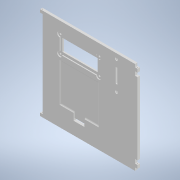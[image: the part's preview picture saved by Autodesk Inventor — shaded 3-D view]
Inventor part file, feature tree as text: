
AUTODESK INVENTOR PART (.ipt)
format: ipt  version: 2020 (Build 240168000, 168)  size: 380,928 bytes
history: native  units: in
note: dims shown in document units (in); Inventor stores cm internally (conversion verified against a paired STEP export)
features: extrude x10, sketch x8, hole x7, fillet x3, plane x2, shell x1, split x1
ambient origin geometry x8: Origin, YZ Plane, XZ Plane, XY Plane, X Axis, Y Axis, Z Axis, Center Point
bodies: Solid1 (feature_tree)
feature tree (32):
  extrude  "Extrusion1"  Depth=7.874in
  shell  "Shell1"  Thickness=7.874in
  extrude  "Extrusion2"  Depth=1.6339in
  sketch  "Sketch3"  dims[d7=6.1024in d8=1.6339in]
  extrude  "Extrusion3"  Depth=1.1811in
  hole  "Hole1"  [1 undecoded]
  fillet  "Fillet2"  Radius=0.8661in
  extrude  "Extrusion4"  Depth=1.1417in
  sketch  "Sketch4"  dims[d9=0.3937in d10=0.0in d12=1.1811in]
  extrude  "Extrusion5"  Depth=0.3937in
  extrude  "Extrusion6"  Depth=2.8346in
  extrude  "Extrusion7"  Depth=0.1575in
  extrude  "Extrusion8"  Depth=0.1575in
  fillet  "Fillet3"  Radius=0.1969in
  fillet  "Fillet4"  Radius=0.1969in
  extrude  "Extrusion9"  Depth=0.3937in
  plane  "Work Plane1"
  extrude  "Extrusion10"  Depth=0.3937in
  plane  "Work Plane2"
  split  "Split1"
  hole  "Hole3"  [1 undecoded]
  hole  "Hole4"  [1 undecoded]
  hole  "Hole5"  [1 undecoded]
  hole  "Hole6"  [1 undecoded]
  hole  "Hole7"  [1 undecoded]
  sketch  "Sketch1"  dims[d0=7.874in d1=7.874in d2=7.874in d3=0.0in]
  sketch  "Sketch5"  dims[d13=1.5748in d16=3.1496in d19=0.8661in]
  sketch  "Sketch6"  dims[d20=0.1575in d22=1.1417in]
  hole  "Hole2"  [1 undecoded]
  sketch  "Sketch7"  dims[d23=0.3937in d24=0.3937in]
  sketch  "Sketch8"  dims[d25=0.0787in d26=0.0in d27=2.8346in]
  sketch  "Sketch9"  dims[d28=0.9843in d29=0.1575in d30=0.1575in d31=0.1969in d32=0.1969in d33=0.3937in d34=0.3937in d35=0.3937in d36=0.1378in d37=0.2362in d38=0.1575in d39=0.0787in d40=90.0deg d41=0.315in d42=0.8108in d43=0.1181in d44=3.937in d45=0.1969in d46=0.0in d47=0.0787in d48=0.0591in d49=3.1496in d50=0.0in d51=2.3622in d52=0.0in d53=1.5748in d54=0.0in d55=0.7874in d56=0.0in d57=0.1181in d58=0.1575in d59=1.5748in d60=0.0in d61=-0.5906in d62=0.9843in d63=0.0in d64=0.0in d67=0.3937in d73=0.1969in d74=0.2362in d75=0.2756in d76=0.315in d77=0.2362in d78=0.2756in d79=0.315in d80=0.1969in d81=0.2362in d82=0.2362in d83=0.0787in d84=0.2362in d85=0.1575in d86=0.0787in d87=90.0deg d88=0.315in d89=0.0in d90=0.5586in d91=0.5586in d92=0.0689in d93=0.0689in d94=0.1575in d95=0.2362in d96=0.2362in d97=0.0787in d98=90.0deg d99=0.5906in d100=0.0in d101=0.0984in d102=0.0984in d103=0.0787in d104=0.2362in d105=0.2362in d106=0.0787in d107=90.0deg d108=0.5906in d109=0.0in d110=0.0984in d111=0.0984in d112=0.0787in d113=0.2362in d114=0.2362in d115=0.0787in d116=90.0deg d117=0.5906in d118=0.0in d119=0.0984in d120=0.0984in d121=0.0787in d122=0.2362in d123=0.2362in d124=0.0787in d125=90.0deg d126=0.5906in d127=0.0in d5=0.0394in d6=0.0394in d11=0.5635in d14=0.0025in d15=0.0295in d65=0.0344in]
note: 7 required parameter values undecoded (feature->parameter linkage not recoverable at this tier; creation-order binding heuristic only, values carry confidence <= 0.55)
